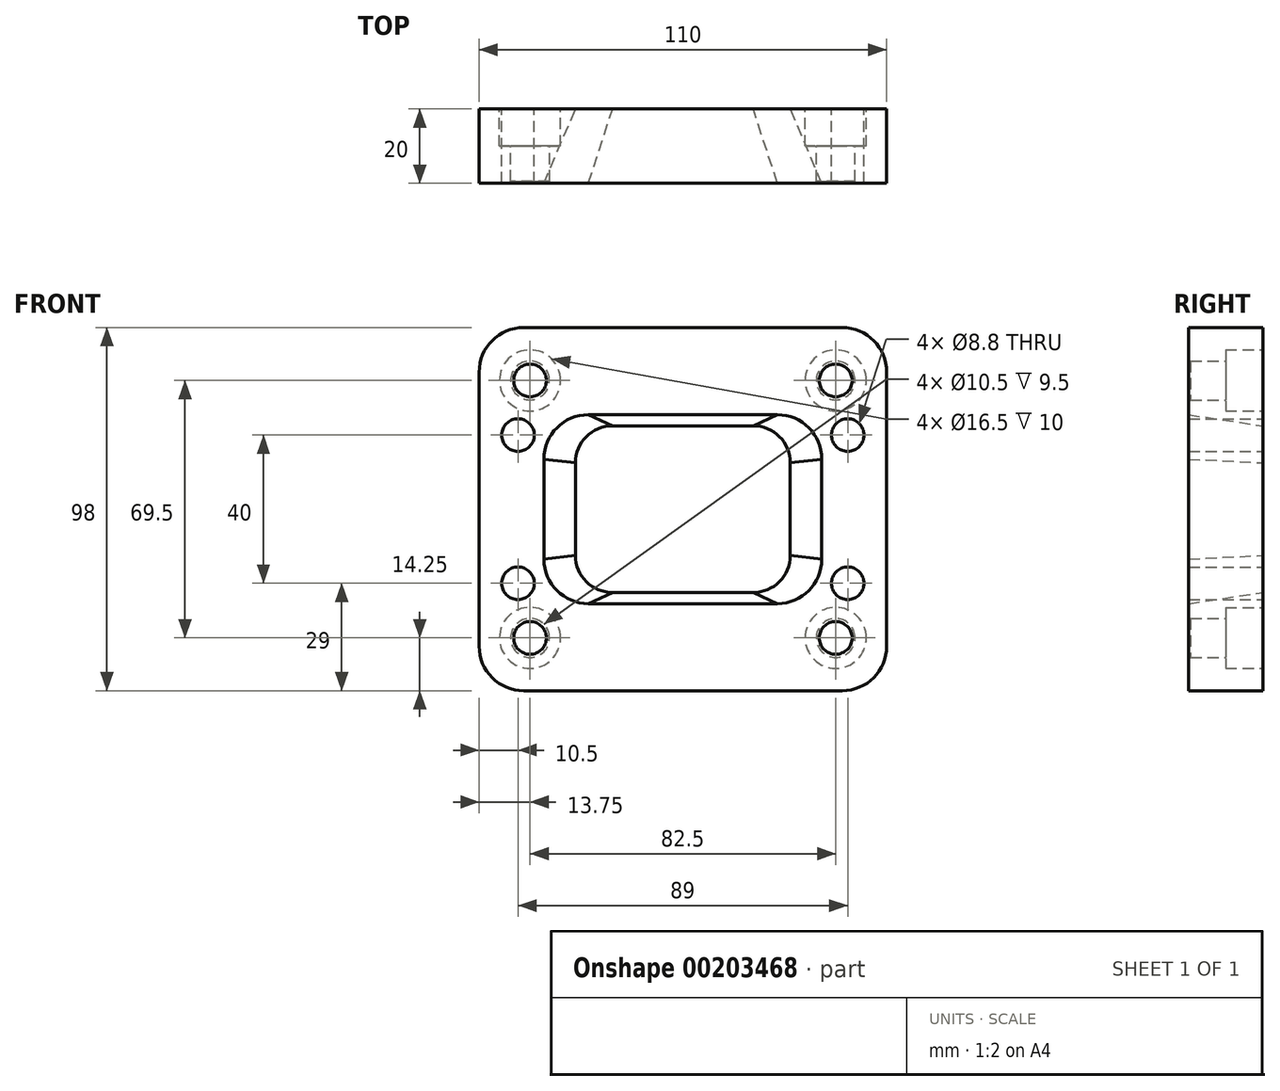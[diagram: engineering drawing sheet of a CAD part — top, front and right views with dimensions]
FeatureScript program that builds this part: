
annotation { "Feature Type Name" : "Feature", "Feature Type Description" : "" }
export const myFeature = defineFeature(function(context is Context, id is Id, definition is map)
    precondition{}
    {
        {
            var Q0;
            Q0=qCreatedBy(makeId("Front.planeOp"),FACE);
            var sketch = newSketch(context, id + "F0", { "sketchPlane" : qUnion([Q0])});
            skLineSegment(sketch, "E0.bottom", {"start": v(-55, -49) * mm, "end": v(55, -49) * mm});
            skLineSegment(sketch, "E0.top", {"start": v(-55, 49) * mm, "end": v(55, 49) * mm});
            skLineSegment(sketch, "E0.left", {"start": v(-55, -49) * mm, "end": v(-55, 49) * mm});
            skLineSegment(sketch, "E0.right", {"start": v(55, -49) * mm, "end": v(55, 49) * mm});
            skPoint(sketch, "E0.middle", {"position": v(0, 0) * mm});
            skSolve(sketch);
        }
        {
            var Q0;
            Q0=makeQuery(id+"F0.imprint","IMPRINT",FACE,{"disambiguationData":[TD([[makeQuery(id+"F0.imprint","IMPRINT",EDGE,{"derivedFrom":sQuery(id+"F0.wireOp",EDGE,"E0.bottom")}),1.0]])]});
            extrude(context, id + "F1", {"entities" : qUnion([Q0]), "depth" : 20 * mm, "symmetric" : true});
        }
        {
            var Q0;
            Q0=makeQuery(id+"F1.opExtrude","CAP_FACE",FACE,{"disambiguationData":[OSD([sQuery(id+"F0.wireOp",EDGE,"E0.bottom"),sQuery(id+"F0.wireOp",EDGE,"E0.top"),sQuery(id+"F0.wireOp",EDGE,"E0.left"),sQuery(id+"F0.wireOp",EDGE,"E0.right")])],"isStart":false});
            var sketch = newSketch(context, id + "F2", { "sketchPlane" : qUnion([Q0])});
            skLineSegment(sketch, "E1.bottom", {"start": v(-25.5, -25.5) * mm, "end": v(25.5, -25.5) * mm});
            skLineSegment(sketch, "E1.top", {"start": v(-25.5, 25.5) * mm, "end": v(25.5, 25.5) * mm});
            skLineSegment(sketch, "E1.left", {"start": v(-37.5, -13.5) * mm, "end": v(-37.5, 13.5) * mm});
            skLineSegment(sketch, "E1.right", {"start": v(37.5, -13.5) * mm, "end": v(37.5, 13.5) * mm});
            skPoint(sketch, "E1.middle", {"position": v(0, 0) * mm});
            skPoint(sketch, "E2.visualSharp", {"position": v(-37.5, 25.5) * mm});
            skArc(sketch, "E2.filletArc", {"start": v(-25.5, 25.5) * mm, "mid": v(-33.99, 21.99) * mm, "end": v(-37.5, 13.5) * mm});
            skPoint(sketch, "E3.visualSharp", {"position": v(-37.5, -25.5) * mm});
            skArc(sketch, "E3.filletArc", {"start": v(-37.5, -13.5) * mm, "mid": v(-33.99, -21.99) * mm, "end": v(-25.5, -25.5) * mm});
            skPoint(sketch, "E4.visualSharp", {"position": v(37.5, -25.5) * mm});
            skArc(sketch, "E4.filletArc", {"start": v(25.5, -25.5) * mm, "mid": v(33.99, -21.99) * mm, "end": v(37.5, -13.5) * mm});
            skPoint(sketch, "E5.visualSharp", {"position": v(37.5, 25.5) * mm});
            skArc(sketch, "E5.filletArc", {"start": v(37.5, 13.5) * mm, "mid": v(33.99, 21.99) * mm, "end": v(25.5, 25.5) * mm});
            skSolve(sketch);
        }
        {
            var Q0;
            Q0=makeQuery(id+"F1.opExtrude","CAP_FACE",FACE,{"disambiguationData":[OSD([sQuery(id+"F0.wireOp",EDGE,"E0.bottom"),sQuery(id+"F0.wireOp",EDGE,"E0.top"),sQuery(id+"F0.wireOp",EDGE,"E0.left"),sQuery(id+"F0.wireOp",EDGE,"E0.right")])],"isStart":true});
            var sketch = newSketch(context, id + "F3", { "sketchPlane" : qUnion([Q0])});
            skLineSegment(sketch, "E6.bottom", {"start": v(-19, -22.5) * mm, "end": v(19, -22.5) * mm});
            skLineSegment(sketch, "E6.top", {"start": v(-19, 22.5) * mm, "end": v(19, 22.5) * mm});
            skLineSegment(sketch, "E6.left", {"start": v(-29, -12.5) * mm, "end": v(-29, 12.5) * mm});
            skLineSegment(sketch, "E6.right", {"start": v(29, -12.5) * mm, "end": v(29, 12.5) * mm});
            skPoint(sketch, "E6.middle", {"position": v(0, 0) * mm});
            skPoint(sketch, "E7", {"position": v(-44.5, 20) * mm});
            skPoint(sketch, "E8", {"position": v(44.5, 20) * mm});
            skPoint(sketch, "E9", {"position": v(44.5, -20) * mm});
            skPoint(sketch, "E10", {"position": v(-44.5, -20) * mm});
            skPoint(sketch, "E11.visualSharp", {"position": v(-29, 22.5) * mm});
            skArc(sketch, "E11.filletArc", {"start": v(-19, 22.5) * mm, "mid": v(-26.07, 19.57) * mm, "end": v(-29, 12.5) * mm});
            skPoint(sketch, "E12.visualSharp", {"position": v(-29, -22.5) * mm});
            skArc(sketch, "E12.filletArc", {"start": v(-29, -12.5) * mm, "mid": v(-26.07, -19.57) * mm, "end": v(-19, -22.5) * mm});
            skPoint(sketch, "E13.visualSharp", {"position": v(29, -22.5) * mm});
            skArc(sketch, "E13.filletArc", {"start": v(19, -22.5) * mm, "mid": v(26.07, -19.57) * mm, "end": v(29, -12.5) * mm});
            skPoint(sketch, "E14.visualSharp", {"position": v(29, 22.5) * mm});
            skArc(sketch, "E14.filletArc", {"start": v(29, 12.5) * mm, "mid": v(26.07, 19.57) * mm, "end": v(19, 22.5) * mm});
            skPoint(sketch, "E15", {"position": v(-41.25, 34.75) * mm});
            skPoint(sketch, "E16", {"position": v(41.25, 34.75) * mm});
            skPoint(sketch, "E17", {"position": v(41.25, -34.75) * mm});
            skPoint(sketch, "E18", {"position": v(-41.25, -34.75) * mm});
            skSolve(sketch);
        }
        {
            var Q1;
            Q1=makeQuery(id+"F2.imprint","IMPRINT",FACE,{"disambiguationData":[TD([[makeQuery(id+"F2.imprint","IMPRINT",EDGE,{"derivedFrom":sQuery(id+"F2.wireOp",EDGE,"E1.bottom")}),1.0]])]});
            var Q2;
            Q2=makeQuery(id+"F3.imprint","IMPRINT",FACE,{"disambiguationData":[TD([[makeQuery(id+"F3.imprint","IMPRINT",EDGE,{"derivedFrom":sQuery(id+"F3.wireOp",EDGE,"E6.bottom")}),1.0]])]});
            loft(context, id + "F4", {"operationType" : NewBodyOperationType.REMOVE, "sheetProfilesArray" : [{ "sheetProfileEntities" : qUnion([Q1]) }, { "sheetProfileEntities" : qUnion([Q2]) }]});
        }
        {
            var Q0;
            Q0=makeQuery(id+"F1.opExtrude","SWEPT_EDGE",EDGE,{"disambiguationData":[OSD([sQuery(id+"F0.wireOp",EDGE,"E0.top"),sQuery(id+"F0.wireOp",EDGE,"E0.left")])]});
            var Q1;
            Q1=makeQuery(id+"F1.opExtrude","SWEPT_EDGE",EDGE,{"disambiguationData":[OSD([sQuery(id+"F0.wireOp",EDGE,"E0.bottom"),sQuery(id+"F0.wireOp",EDGE,"E0.left")])]});
            var Q2;
            Q2=makeQuery(id+"F1.opExtrude","SWEPT_EDGE",EDGE,{"disambiguationData":[OSD([sQuery(id+"F0.wireOp",EDGE,"E0.bottom"),sQuery(id+"F0.wireOp",EDGE,"E0.right")])]});
            var Q3;
            Q3=makeQuery(id+"F1.opExtrude","SWEPT_EDGE",EDGE,{"disambiguationData":[OSD([sQuery(id+"F0.wireOp",EDGE,"E0.top"),sQuery(id+"F0.wireOp",EDGE,"E0.right")])]});
            fillet(context, id + "F5", {"entities" : qUnion([Q0, Q1, Q2, Q3]), "radius" : 12 * mm, "tangentPropagation" : true, "allowEdgeOverflow" : false});
        }
        {
            var Q0;
            Q0=sQuery(id+"F3.wireOp",VERTEX,"E7");
            var Q1;
            Q1=sQuery(id+"F3.wireOp",VERTEX,"E10");
            var Q2;
            Q2=sQuery(id+"F3.wireOp",VERTEX,"E9");
            var Q3;
            Q3=sQuery(id+"F3.wireOp",VERTEX,"E8");
            var Q4;
            Q4=makeQuery(id+"F1.opExtrude","SWEPT_BODY",BODY,{"disambiguationData":[OSD([sQuery(id+"F0.wireOp",EDGE,"E0.bottom"),sQuery(id+"F0.wireOp",EDGE,"E0.top"),sQuery(id+"F0.wireOp",EDGE,"E0.left"),sQuery(id+"F0.wireOp",EDGE,"E0.right")])]});
            hole(context, id + "F6", {"style" : HoleStyle.SIMPLE, "endStyle" : HoleEndStyle.BLIND, "standardTappedOrClearance" : lookupTablePath({ "standard" : "ISO", "engagement" : "75%", "pitch" : "1.25 mm", "size" : "M10", "type" : "Tapped" }), "standardBlindInLast" : lookupTablePath({ "standard" : "ISO", "engagement" : "75%", "pitch" : "1.25 mm", "size" : "M10", "type" : "Tapped" }), "holeDiameter" : 8.8 * mm, "holeDepth" : 20 * mm, "startFromSketch" : true, "locations" : qUnion([Q0, Q1, Q2, Q3]), "scope" : qUnion([Q4]), "majorDiameter" : 10 * mm});
        }
        {
            var Q0;
            Q0=sQuery(id+"F3.wireOp",VERTEX,"E15");
            var Q1;
            Q1=sQuery(id+"F3.wireOp",VERTEX,"E16");
            var Q2;
            Q2=sQuery(id+"F3.wireOp",VERTEX,"E18");
            var Q3;
            Q3=sQuery(id+"F3.wireOp",VERTEX,"E17");
            var Q4;
            Q4=makeQuery(id+"F1.opExtrude","SWEPT_BODY",BODY,{"disambiguationData":[OSD([sQuery(id+"F0.wireOp",EDGE,"E0.bottom"),sQuery(id+"F0.wireOp",EDGE,"E0.top"),sQuery(id+"F0.wireOp",EDGE,"E0.left"),sQuery(id+"F0.wireOp",EDGE,"E0.right")])]});
            hole(context, id + "F7", {"style" : HoleStyle.C_BORE, "endStyle" : HoleEndStyle.BLIND, "holeDiameter" : 10.5 * mm, "cBoreDiameter" : 16.5 * mm, "cBoreDepth" : 10 * mm, "holeDepth" : 19.5 * mm, "startFromSketch" : true, "locations" : qUnion([Q0, Q1, Q2, Q3]), "scope" : qUnion([Q4])});
        }
    });
